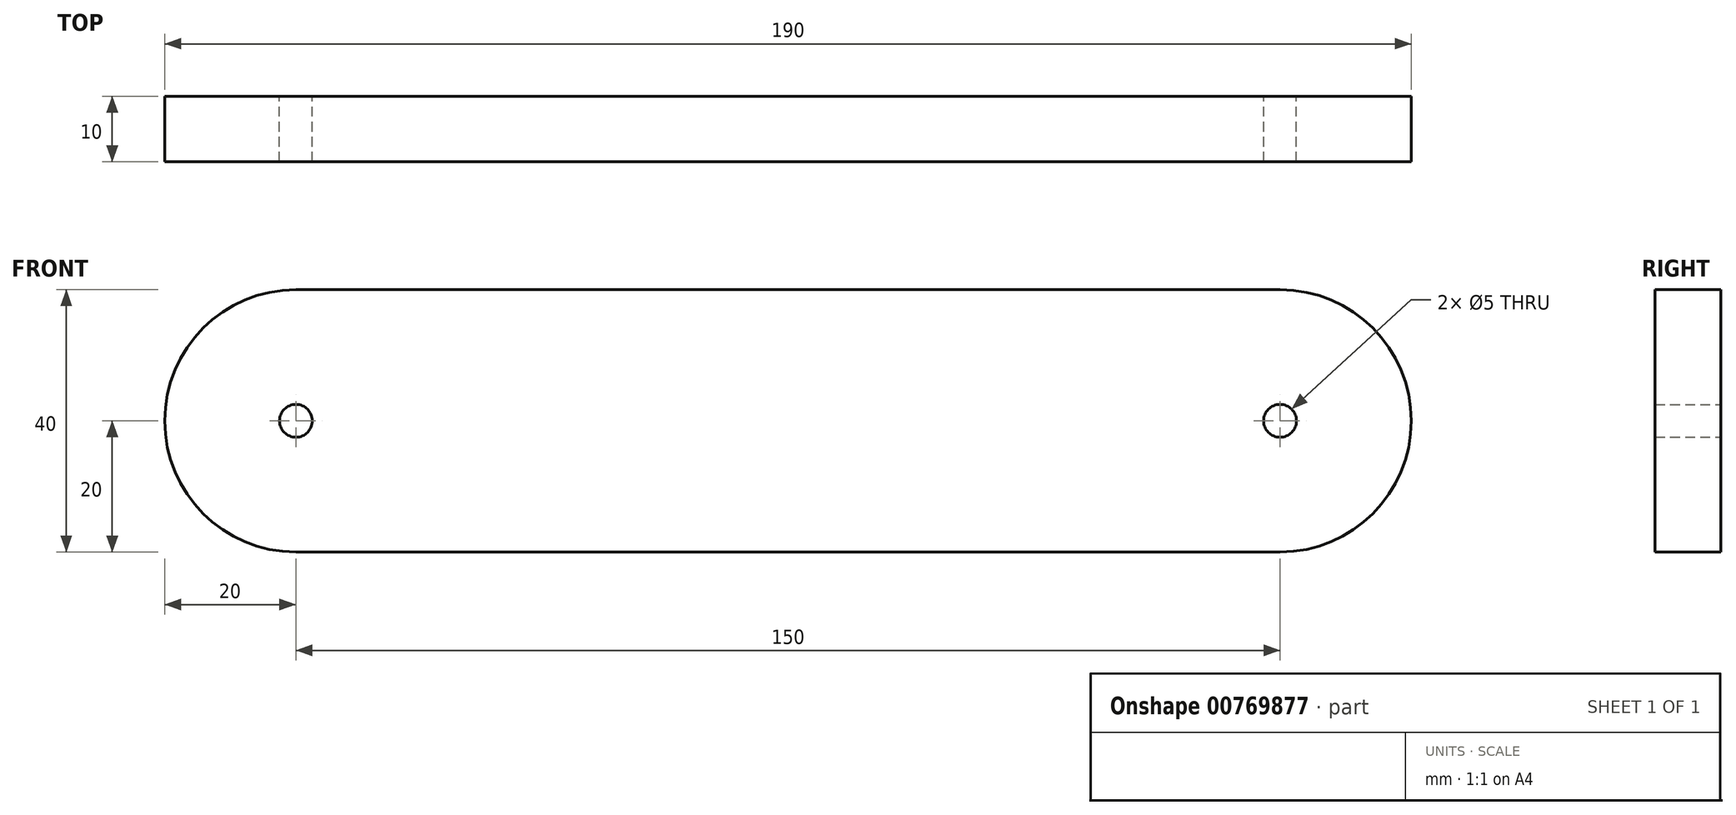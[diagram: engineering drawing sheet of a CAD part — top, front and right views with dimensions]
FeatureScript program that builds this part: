
annotation { "Feature Type Name" : "Feature", "Feature Type Description" : "" }
export const myFeature = defineFeature(function(context is Context, id is Id, definition is map)
    precondition{}
    {
        {
            var Q0;
            Q0=qCreatedBy(makeId("Front.planeOp"),FACE);
            var sketch = newSketch(context, id + "F0", { "sketchPlane" : qUnion([Q0])});
            skLineSegment(sketch, "E0", {"start": v(0, 0) * mm, "end": v(150, 0) * mm, "construction": true});
            skCircle(sketch, "E1", {"center": v(0, 0) * mm, "radius": 2.5 * mm});
            skCircle(sketch, "E2", {"center": v(150, 0) * mm, "radius": 2.5 * mm});
            skArc(sketch, "E3", {"start": v(0, 20) * mm, "mid": v(-20, 0) * mm, "end": v(0, -20) * mm});
            skArc(sketch, "E4", {"start": v(150, -20) * mm, "mid": v(170, 0) * mm, "end": v(150, 20) * mm});
            skLineSegment(sketch, "E5", {"start": v(0, 20) * mm, "end": v(150, 20) * mm});
            skLineSegment(sketch, "E6.MirrorCS", {"start": v(0, -20) * mm, "end": v(150, -20) * mm});
            skSolve(sketch);
        }
        {
            var Q0;
            Q0 = qSketchRegion(id + "F0", true);
            extrude(context, id + "F1", {"entities" : qUnion([Q0]), "depth" : 10 * mm, "offsetDistance" : 25 * mm});
        }
    });
